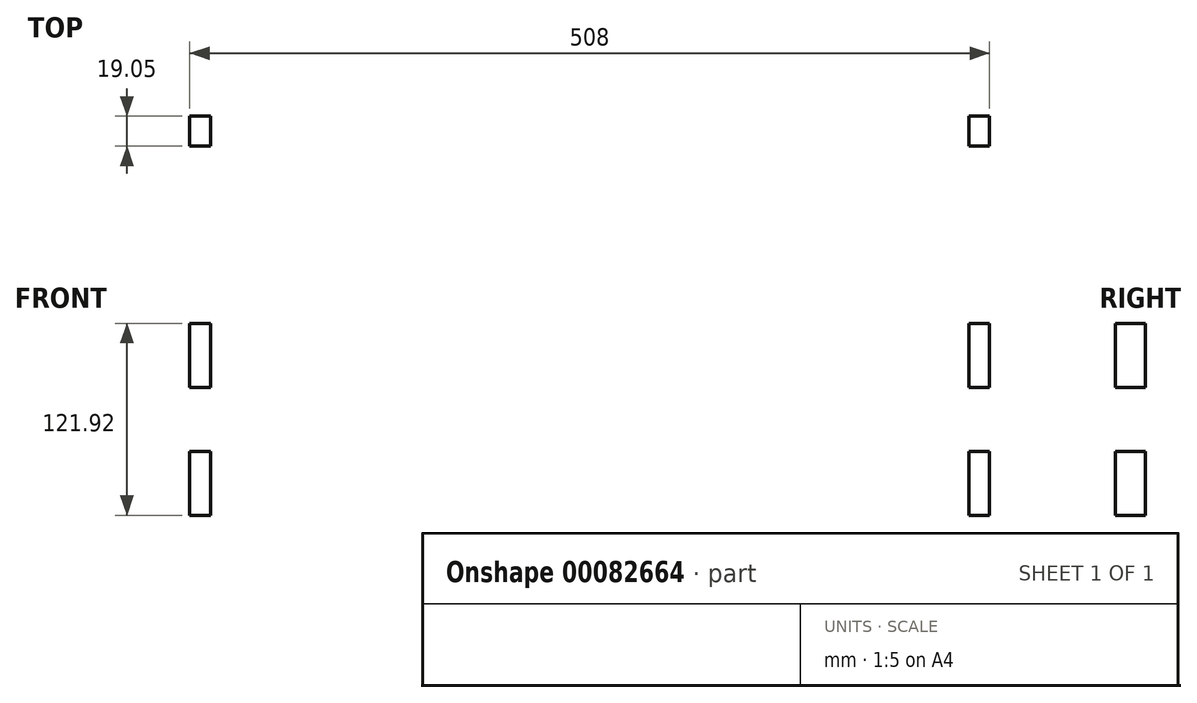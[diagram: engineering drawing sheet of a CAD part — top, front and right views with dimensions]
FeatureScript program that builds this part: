
annotation { "Feature Type Name" : "Feature", "Feature Type Description" : "" }
export const myFeature = defineFeature(function(context is Context, id is Id, definition is map)
    precondition{}
    {
        {
            var Q0;
            Q0=qCreatedBy(makeId("Front.planeOp"),FACE);
            var sketch = newSketch(context, id + "F0", { "sketchPlane" : qUnion([Q0])});
            skLineSegment(sketch, "E0", {"start": v(-128.3, 67.17) * mm, "end": v(379.7, 67.17) * mm});
            skLineSegment(sketch, "E1", {"start": v(-128.3, 67.17) * mm, "end": v(-128.3, -101.1) * mm});
            skLineSegment(sketch, "E2", {"start": v(-128.3, -101.1) * mm, "end": v(379.7, -101.1) * mm});
            skLineSegment(sketch, "E3", {"start": v(379.7, 67.17) * mm, "end": v(379.7, -101.1) * mm});
            skLineSegment(sketch, "E4.bottom", {"start": v(-128.3, 67.17) * mm, "end": v(-115.1, 67.17) * mm});
            skLineSegment(sketch, "E4.top", {"start": v(-128.3, 26.53) * mm, "end": v(-115.1, 26.53) * mm});
            skLineSegment(sketch, "E4.left", {"start": v(-128.3, 67.17) * mm, "end": v(-128.3, 26.53) * mm});
            skLineSegment(sketch, "E4.right", {"start": v(-115.1, 67.17) * mm, "end": v(-115.1, 26.53) * mm});
            skLineSegment(sketch, "E5", {"start": v(125.7, 67.17) * mm, "end": v(125.7, -101.1) * mm, "construction": true});
            skLineSegment(sketch, "E6.top", {"start": v(-128.3, -14.1) * mm, "end": v(-115.1, -14.1) * mm});
            skLineSegment(sketch, "E6.left", {"start": v(-128.3, 26.53) * mm, "end": v(-128.3, -14.1) * mm});
            skLineSegment(sketch, "E6.right", {"start": v(-115.1, 26.53) * mm, "end": v(-115.1, -14.1) * mm});
            skLineSegment(sketch, "E7.top", {"start": v(-128.3, -54.75) * mm, "end": v(-115.1, -54.75) * mm});
            skLineSegment(sketch, "E7.left", {"start": v(-128.3, -14.1) * mm, "end": v(-128.3, -54.75) * mm});
            skLineSegment(sketch, "E7.right", {"start": v(-115.1, -14.1) * mm, "end": v(-115.1, -54.75) * mm});
            skLineSegment(sketch, "E8", {"start": v(-115.1, -101.1) * mm, "end": v(-115.1, -54.75) * mm});
            skLineSegment(sketch, "E9", {"start": v(-128.3, -101.1) * mm, "end": v(-115.1, -101.1) * mm});
            skLineSegment(sketch, "E10.MirrorCS", {"start": v(379.7, -14.1) * mm, "end": v(366.5, -14.1) * mm});
            skLineSegment(sketch, "E11.MirrorCS", {"start": v(379.7, 26.53) * mm, "end": v(366.5, 26.53) * mm});
            skLineSegment(sketch, "E12.MirrorCS", {"start": v(379.7, 67.17) * mm, "end": v(366.5, 67.17) * mm});
            skLineSegment(sketch, "E13.MirrorCS", {"start": v(379.7, -101.1) * mm, "end": v(366.5, -101.1) * mm});
            skLineSegment(sketch, "E14.MirrorCS", {"start": v(379.7, -54.75) * mm, "end": v(366.5, -54.75) * mm});
            skLineSegment(sketch, "E15.MirrorCS", {"start": v(379.7, -14.1) * mm, "end": v(379.7, -54.75) * mm});
            skLineSegment(sketch, "E16.MirrorCS", {"start": v(366.5, -14.1) * mm, "end": v(366.5, -54.75) * mm});
            skLineSegment(sketch, "E17.MirrorCS", {"start": v(366.5, -101.1) * mm, "end": v(366.5, -54.75) * mm});
            skLineSegment(sketch, "E18.MirrorCS", {"start": v(366.5, 26.53) * mm, "end": v(366.5, -14.1) * mm});
            skLineSegment(sketch, "E19.MirrorCS", {"start": v(379.7, 67.17) * mm, "end": v(379.7, 26.53) * mm});
            skLineSegment(sketch, "E20.MirrorCS", {"start": v(366.5, 67.17) * mm, "end": v(366.5, 26.53) * mm});
            skLineSegment(sketch, "E21.MirrorCS", {"start": v(379.7, 26.53) * mm, "end": v(379.7, -14.1) * mm});
            skSolve(sketch);
        }
        {
            var Q0;
            Q0=makeQuery(id+"F0.imprint","IMPRINT",FACE,{"disambiguationData":[TD([[makeQuery(id+"F0.imprint","IMPRINT",EDGE,{"derivedFrom":sQuery(id+"F0.wireOp",EDGE,"E4.bottom")}),-1.0]])]});
            var Q1;
            Q1=makeQuery(id+"F0.imprint","IMPRINT",FACE,{"disambiguationData":[TD([[makeQuery(id+"F0.imprint","IMPRINT",EDGE,{"derivedFrom":sQuery(id+"F0.wireOp",EDGE,"E11.MirrorCS")}),-1.0]])]});
            var Q2;
            Q2=makeQuery(id+"F0.imprint","IMPRINT",FACE,{"disambiguationData":[TD([[makeQuery(id+"F0.imprint","IMPRINT",EDGE,{"derivedFrom":sQuery(id+"F0.wireOp",EDGE,"E6.top")}),-1.0]])]});
            var Q3;
            {var subQ0=sQuery(id+"F0.wireOp",EDGE,"E10.MirrorCS");Q3=makeQuery(id+"F0.imprint","IMPRINT",FACE,{"disambiguationData":[TD([[makeQuery(id+"F0.imprint","IMPRINT",EDGE,{"derivedFrom":subQ0}),1.0]])]});}
            var Q4;
            Q4=makeQuery(id+"F0.imprint","IMPRINT",FACE,{"disambiguationData":[TD([[makeQuery(id+"F0.imprint","IMPRINT",EDGE,{"derivedFrom":sQuery(id+"F0.wireOp",EDGE,"E0")}),-1.0]])]});
            extrude(context, id + "F1", {"entities" : qUnion([Q0, Q1, Q2, Q3, Q4]), "depth" : 19.05 * mm});
        }
    });
